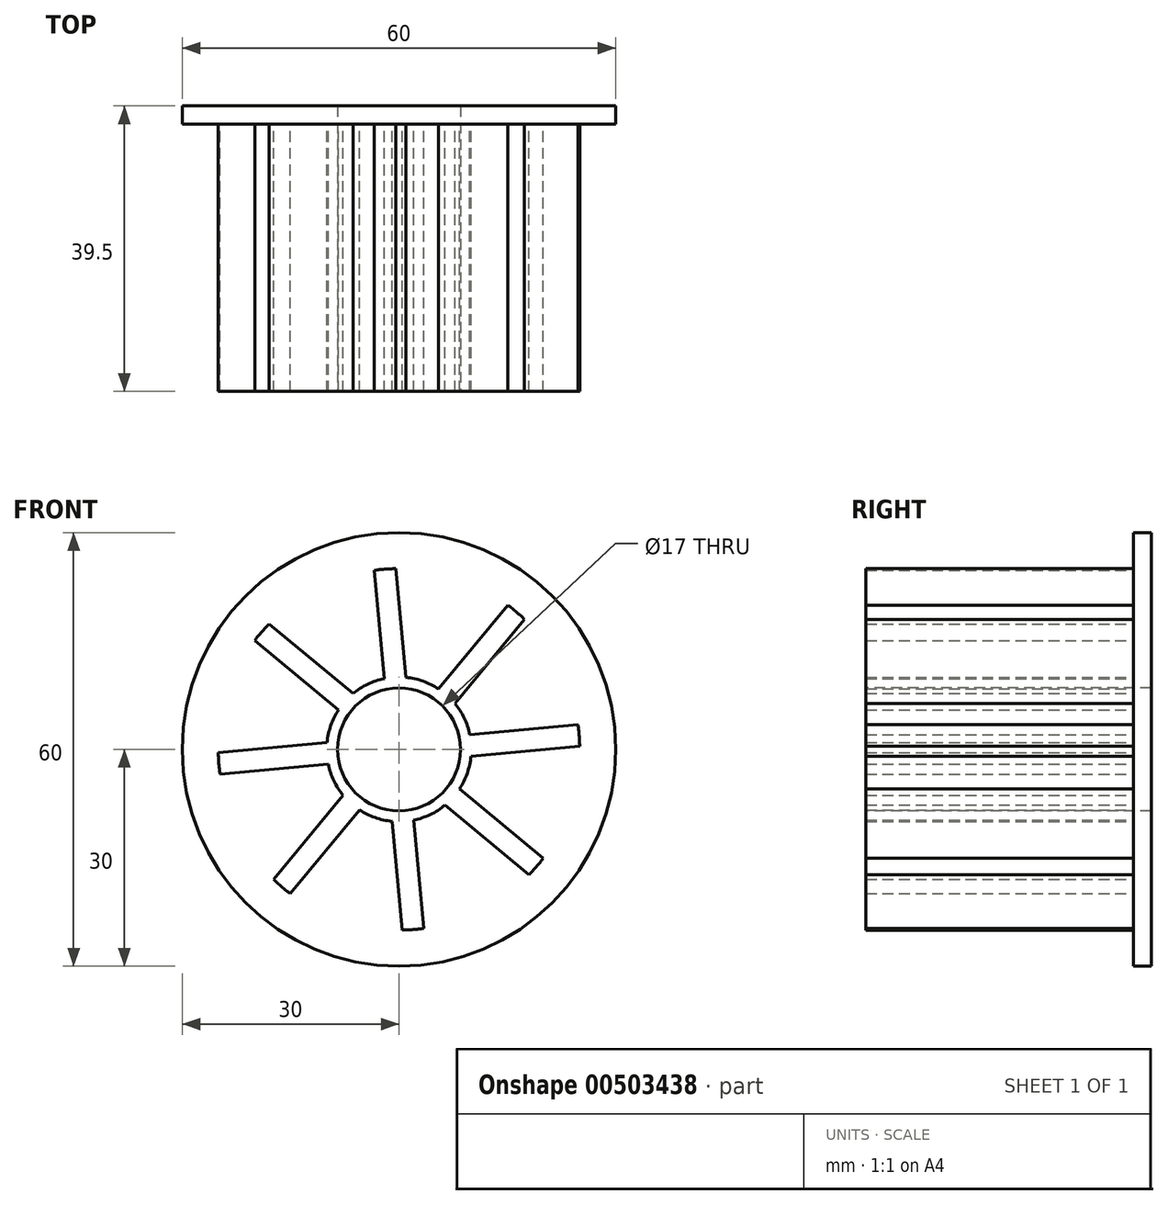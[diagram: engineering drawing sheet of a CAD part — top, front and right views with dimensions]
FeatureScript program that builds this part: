
annotation { "Feature Type Name" : "Feature", "Feature Type Description" : "" }
export const myFeature = defineFeature(function(context is Context, id is Id, definition is map)
    precondition{}
    {
        {
            var Q0;
            Q0=qCreatedBy(makeId("Front.planeOp"),FACE);
            var sketch = newSketch(context, id + "F0", { "sketchPlane" : qUnion([Q0])});
            skCircle(sketch, "E0", {"center": v(0, 0) * mm, "radius": 30 * mm});
            skCircle(sketch, "E1", {"center": v(0, 0) * mm, "radius": 8.5 * mm});
            skSolve(sketch);
        }
        {
            var Q0;
            Q0=qSketchRegion(id+"F0",true);
            extrude(context, id + "F1", {"entities" : qUnion([Q0]), "oppositeDirection" : true, "depth" : 2.5 * mm});
        }
        {
            var Q0;
            Q0=qCreatedBy(makeId("Front.planeOp"),FACE);
            var sketch = newSketch(context, id + "F2", { "sketchPlane" : qUnion([Q0])});
            skCircle(sketch, "E2", {"center": v(0, 0) * mm, "radius": 10 * mm});
            skArc(sketch, "E3", {"start": v(18, -17.36) * mm, "mid": v(19, -16.24) * mm, "end": v(19.94, -15.07) * mm});
            skLineSegment(sketch, "E4", {"start": v(18, -17.36) * mm, "end": v(6.36, -7.72) * mm});
            skLineSegment(sketch, "E5", {"start": v(19.94, -15.07) * mm, "end": v(8.36, -5.48) * mm});
            skLineSegment(sketch, "E6.1.0", {"start": v(24.76, 3.44) * mm, "end": v(9.8, 2.04) * mm});
            skLineSegment(sketch, "E6.1.1", {"start": v(25, 0.45) * mm, "end": v(9.95, -0.96) * mm});
            skArc(sketch, "E6.1.2", {"start": v(25, 0.45) * mm, "mid": v(24.92, 1.95) * mm, "end": v(24.76, 3.44) * mm});
            skLineSegment(sketch, "E6.2.0", {"start": v(15.07, 19.94) * mm, "end": v(5.48, 8.36) * mm});
            skLineSegment(sketch, "E6.2.1", {"start": v(17.36, 18) * mm, "end": v(7.72, 6.36) * mm});
            skArc(sketch, "E6.2.2", {"start": v(17.36, 18) * mm, "mid": v(16.24, 19) * mm, "end": v(15.07, 19.94) * mm});
            skLineSegment(sketch, "E6.3.0", {"start": v(-3.44, 24.76) * mm, "end": v(-2.04, 9.8) * mm});
            skLineSegment(sketch, "E6.3.1", {"start": v(-0.45, 25) * mm, "end": v(0.96, 9.95) * mm});
            skArc(sketch, "E6.3.2", {"start": v(-0.45, 25) * mm, "mid": v(-1.95, 24.92) * mm, "end": v(-3.44, 24.76) * mm});
            skLineSegment(sketch, "E6.4.0", {"start": v(-19.94, 15.07) * mm, "end": v(-8.36, 5.48) * mm});
            skLineSegment(sketch, "E6.4.1", {"start": v(-18, 17.36) * mm, "end": v(-6.36, 7.72) * mm});
            skArc(sketch, "E6.4.2", {"start": v(-18, 17.36) * mm, "mid": v(-19, 16.24) * mm, "end": v(-19.94, 15.07) * mm});
            skLineSegment(sketch, "E6.5.0", {"start": v(-24.76, -3.44) * mm, "end": v(-9.8, -2.04) * mm});
            skLineSegment(sketch, "E6.5.1", {"start": v(-25, -0.45) * mm, "end": v(-9.95, 0.96) * mm});
            skArc(sketch, "E6.5.2", {"start": v(-25, -0.45) * mm, "mid": v(-24.92, -1.95) * mm, "end": v(-24.76, -3.44) * mm});
            skLineSegment(sketch, "E6.6.0", {"start": v(-15.07, -19.94) * mm, "end": v(-5.48, -8.36) * mm});
            skLineSegment(sketch, "E6.6.1", {"start": v(-17.36, -18) * mm, "end": v(-7.72, -6.36) * mm});
            skArc(sketch, "E6.6.2", {"start": v(-17.36, -18) * mm, "mid": v(-16.24, -19) * mm, "end": v(-15.07, -19.94) * mm});
            skLineSegment(sketch, "E6.7.0", {"start": v(3.44, -24.76) * mm, "end": v(2.04, -9.8) * mm});
            skLineSegment(sketch, "E6.7.1", {"start": v(0.45, -25) * mm, "end": v(-0.96, -9.95) * mm});
            skArc(sketch, "E6.7.2", {"start": v(0.45, -25) * mm, "mid": v(1.95, -24.92) * mm, "end": v(3.44, -24.76) * mm});
            skSolve(sketch);
        }
        {
            var Q0;
            {var subQ0=sQuery(id+"F2.wireOp",EDGE,"E2");var subQ8=makeQuery(id+"F2.imprint","INTERSECT",VERTEX,{"derivedFrom":[subQ0,sQuery(id+"F2.wireOp",EDGE,"E6.1.0")]});Q0=makeQuery(id+"F2.imprint","IMPRINT",FACE,{"disambiguationData":[TD([[makeQuery(id+"F2.imprint","IMPRINT",EDGE,{"disambiguationData":[TD([[subQ8,-1.0]])],"derivedFrom":subQ0}),1.0]])]});}
            var Q1;
            {var subQ0=sQuery(id+"F2.wireOp",EDGE,"E6.4.0");Q1=makeQuery(id+"F2.imprint","IMPRINT",FACE,{"disambiguationData":[TD([[makeQuery(id+"F2.imprint","IMPRINT",EDGE,{"derivedFrom":subQ0}),1.0]])]});}
            var Q2;
            {var subQ0=sQuery(id+"F2.wireOp",EDGE,"E6.6.0");Q2=makeQuery(id+"F2.imprint","IMPRINT",FACE,{"disambiguationData":[TD([[makeQuery(id+"F2.imprint","IMPRINT",EDGE,{"derivedFrom":subQ0}),1.0]])]});}
            var Q3;
            {var subQ0=sQuery(id+"F2.wireOp",EDGE,"E6.7.0");Q3=makeQuery(id+"F2.imprint","IMPRINT",FACE,{"disambiguationData":[TD([[makeQuery(id+"F2.imprint","IMPRINT",EDGE,{"derivedFrom":subQ0}),1.0]])]});}
            var Q4;
            Q4=makeQuery(id+"F2.imprint","IMPRINT",FACE,{"disambiguationData":[TD([[makeQuery(id+"F2.imprint","IMPRINT",EDGE,{"derivedFrom":sQuery(id+"F2.wireOp",EDGE,"E3")}),1.0]])]});
            var Q5;
            {var subQ0=sQuery(id+"F2.wireOp",EDGE,"E6.1.0");Q5=makeQuery(id+"F2.imprint","IMPRINT",FACE,{"disambiguationData":[TD([[makeQuery(id+"F2.imprint","IMPRINT",EDGE,{"derivedFrom":subQ0}),1.0]])]});}
            var Q6;
            {var subQ0=sQuery(id+"F2.wireOp",EDGE,"E6.2.0");Q6=makeQuery(id+"F2.imprint","IMPRINT",FACE,{"disambiguationData":[TD([[makeQuery(id+"F2.imprint","IMPRINT",EDGE,{"derivedFrom":subQ0}),1.0]])]});}
            var Q7;
            {var subQ0=sQuery(id+"F2.wireOp",EDGE,"E6.3.0");Q7=makeQuery(id+"F2.imprint","IMPRINT",FACE,{"disambiguationData":[TD([[makeQuery(id+"F2.imprint","IMPRINT",EDGE,{"derivedFrom":subQ0}),1.0]])]});}
            var Q8;
            {var subQ0=sQuery(id+"F2.wireOp",EDGE,"E6.5.0");Q8=makeQuery(id+"F2.imprint","IMPRINT",FACE,{"disambiguationData":[TD([[makeQuery(id+"F2.imprint","IMPRINT",EDGE,{"derivedFrom":subQ0}),1.0]])]});}
            extrude(context, id + "F3", {"entities" : qUnion([Q0, Q1, Q2, Q3, Q4, Q5, Q6, Q7, Q8]), "operationType" : NewBodyOperationType.ADD, "depth" : 37 * mm});
        }
        {
            var Q0;
            Q0=makeQuery(id+"F3.opExtrude","CAP_FACE",FACE,{"disambiguationData":[OSD([sQuery(id+"F2.wireOp",EDGE,"E2"),sQuery(id+"F2.wireOp",EDGE,"E3"),sQuery(id+"F2.wireOp",EDGE,"E4"),sQuery(id+"F2.wireOp",EDGE,"E5"),sQuery(id+"F2.wireOp",EDGE,"E6.1.0"),sQuery(id+"F2.wireOp",EDGE,"E6.1.1"),sQuery(id+"F2.wireOp",EDGE,"E6.1.2"),sQuery(id+"F2.wireOp",EDGE,"E6.2.0"),sQuery(id+"F2.wireOp",EDGE,"E6.2.1"),sQuery(id+"F2.wireOp",EDGE,"E6.2.2"),sQuery(id+"F2.wireOp",EDGE,"E6.3.0"),sQuery(id+"F2.wireOp",EDGE,"E6.3.1"),sQuery(id+"F2.wireOp",EDGE,"E6.3.2"),sQuery(id+"F2.wireOp",EDGE,"E6.4.0"),sQuery(id+"F2.wireOp",EDGE,"E6.4.1"),sQuery(id+"F2.wireOp",EDGE,"E6.4.2"),sQuery(id+"F2.wireOp",EDGE,"E6.5.0"),sQuery(id+"F2.wireOp",EDGE,"E6.5.1"),sQuery(id+"F2.wireOp",EDGE,"E6.5.2"),sQuery(id+"F2.wireOp",EDGE,"E6.6.0"),sQuery(id+"F2.wireOp",EDGE,"E6.6.1"),sQuery(id+"F2.wireOp",EDGE,"E6.6.2"),sQuery(id+"F2.wireOp",EDGE,"E6.7.0"),sQuery(id+"F2.wireOp",EDGE,"E6.7.1"),sQuery(id+"F2.wireOp",EDGE,"E6.7.2")])],"isStart":true});
            extrude(context, id + "F4", {"entities" : qUnion([Q0]), "operationType" : NewBodyOperationType.REMOVE, "oppositeDirection" : true, "depth" : 40 * mm});
        }
    });
